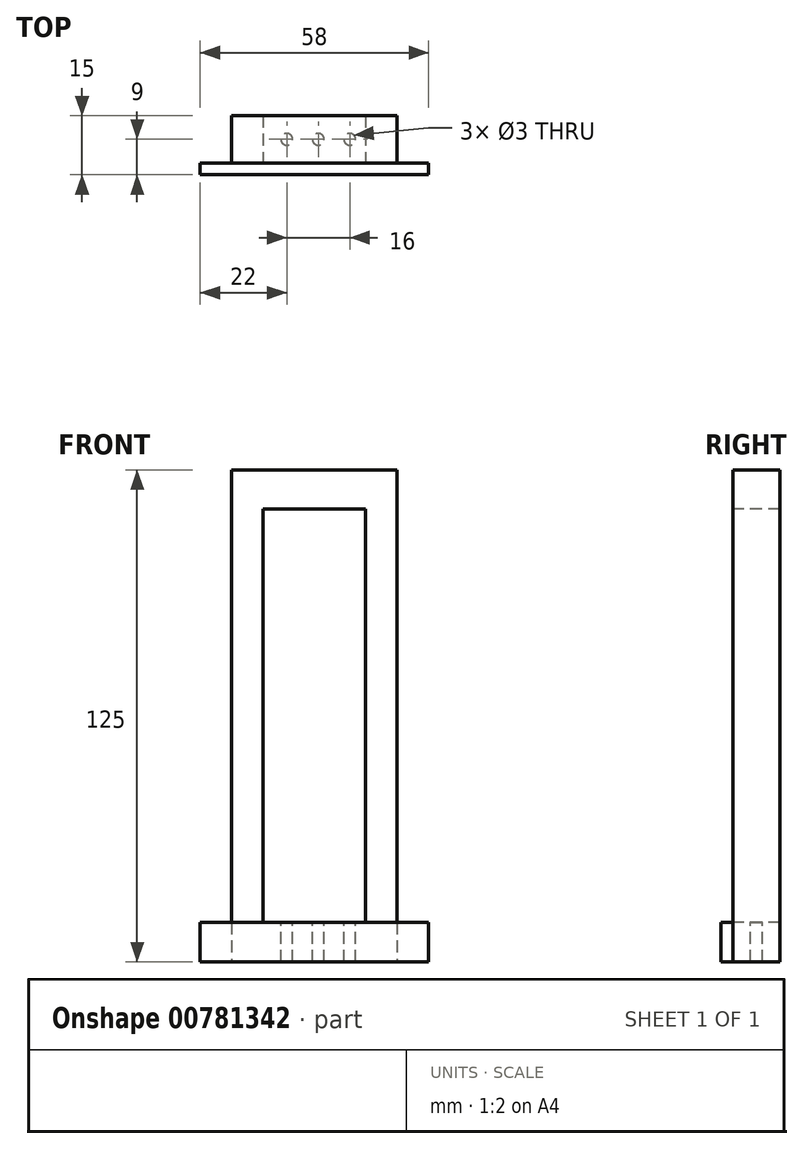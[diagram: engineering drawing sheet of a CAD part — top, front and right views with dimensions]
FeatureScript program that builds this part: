
annotation { "Feature Type Name" : "Feature", "Feature Type Description" : "" }
export const myFeature = defineFeature(function(context is Context, id is Id, definition is map)
    precondition{}
    {
        {
            var Q0;
            Q0=qCreatedBy(makeId("Top.planeOp"),FACE);
            var sketch = newSketch(context, id + "F0", { "sketchPlane" : qUnion([Q0])});
            skLineSegment(sketch, "E0.bottom", {"start": v(21, 6) * mm, "end": v(-21, 6) * mm});
            skLineSegment(sketch, "E0.top", {"start": v(21, -6) * mm, "end": v(-21, -6) * mm});
            skLineSegment(sketch, "E0.left", {"start": v(21, 6) * mm, "end": v(21, -6) * mm});
            skLineSegment(sketch, "E0.right", {"start": v(-21, 6) * mm, "end": v(-21, -6) * mm});
            skPoint(sketch, "E0.middle", {"position": v(0, 0) * mm});
            skSolve(sketch);
        }
        {
            var Q0;
            Q0 = qSketchRegion(id + "F0", true);
            extrude(context, id + "F1", {"entities" : qUnion([Q0]), "depth" : 10 * mm, "offsetDistance" : 25 * mm});
        }
        {
            var Q0;
            Q0=makeQuery(id+"F1.opExtrude","CAP_FACE",FACE,{"disambiguationData":[OSD([sQuery(id+"F0.wireOp",EDGE,"E0.bottom"),sQuery(id+"F0.wireOp",EDGE,"E0.top"),sQuery(id+"F0.wireOp",EDGE,"E0.left"),sQuery(id+"F0.wireOp",EDGE,"E0.right")])],"isStart":false});
            var sketch = newSketch(context, id + "F2", { "sketchPlane" : qUnion([Q0])});
            skLineSegment(sketch, "E1.bottom", {"start": v(-21, 6) * mm, "end": v(-13, 6) * mm});
            skLineSegment(sketch, "E1.top", {"start": v(-21, -6) * mm, "end": v(-13, -6) * mm});
            skLineSegment(sketch, "E1.left", {"start": v(-21, 6) * mm, "end": v(-21, -6) * mm});
            skLineSegment(sketch, "E1.right", {"start": v(-13, 6) * mm, "end": v(-13, -6) * mm});
            skLineSegment(sketch, "E2.bottom", {"start": v(21, 6) * mm, "end": v(13, 6) * mm});
            skLineSegment(sketch, "E2.top", {"start": v(21, -6) * mm, "end": v(13, -6) * mm});
            skLineSegment(sketch, "E2.left", {"start": v(21, 6) * mm, "end": v(21, -6) * mm});
            skLineSegment(sketch, "E2.right", {"start": v(13, 6) * mm, "end": v(13, -6) * mm});
            skSolve(sketch);
        }
        {
            var Q0;
            Q0 = qSketchRegion(id + "F2", true);
            extrude(context, id + "F3", {"entities" : qUnion([Q0]), "operationType" : NewBodyOperationType.ADD, "depth" : 105 * mm, "offsetDistance" : 25 * mm});
        }
        {
            var Q0;
            Q0=makeQuery(id+"F3.opExtrude","CAP_FACE",FACE,{"disambiguationData":[OSD([sQuery(id+"F2.wireOp",EDGE,"E1.bottom"),sQuery(id+"F2.wireOp",EDGE,"E1.top"),sQuery(id+"F2.wireOp",EDGE,"E1.left"),sQuery(id+"F2.wireOp",EDGE,"E1.right")])],"isStart":false});
            var sketch = newSketch(context, id + "F4", { "sketchPlane" : qUnion([Q0])});
            skLineSegment(sketch, "E3.bottom", {"start": v(-21, 6) * mm, "end": v(21, 6) * mm});
            skLineSegment(sketch, "E3.top", {"start": v(-21, -6) * mm, "end": v(21, -6) * mm});
            skLineSegment(sketch, "E3.left", {"start": v(-21, 6) * mm, "end": v(-21, -6) * mm});
            skLineSegment(sketch, "E3.right", {"start": v(21, 6) * mm, "end": v(21, -6) * mm});
            skSolve(sketch);
        }
        {
            var Q0;
            Q0 = qSketchRegion(id + "F4", true);
            extrude(context, id + "F5", {"entities" : qUnion([Q0]), "operationType" : NewBodyOperationType.ADD, "depth" : 10 * mm, "offsetDistance" : 25 * mm});
        }
        {
            var Q0;
            Q0=makeQuery(id+"F5.boolean.opBoolean","MERGE",FACE,{"derivedFrom":[makeQuery(id+"F3.boolean.opBoolean","MERGE",FACE,{"derivedFrom":[makeQuery(id+"F1.opExtrude","SWEPT_FACE",FACE,{"disambiguationData":[OSD([sQuery(id+"F0.wireOp",EDGE,"E0.top")])]}),makeQuery(id+"F3.opExtrude","SWEPT_FACE",FACE,{"disambiguationData":[OSD([sQuery(id+"F2.wireOp",EDGE,"E1.top")])]}),makeQuery(id+"F3.opExtrude","SWEPT_FACE",FACE,{"disambiguationData":[OSD([sQuery(id+"F2.wireOp",EDGE,"E2.top")])]})]}),makeQuery(id+"F5.opExtrude","SWEPT_FACE",FACE,{"disambiguationData":[OSD([sQuery(id+"F4.wireOp",EDGE,"E3.top")])]})]});
            var sketch = newSketch(context, id + "F6", { "sketchPlane" : qUnion([Q0])});
            skLineSegment(sketch, "E4.bottom", {"start": v(-29, 0) * mm, "end": v(29, 0) * mm});
            skLineSegment(sketch, "E4.top", {"start": v(-29, 10) * mm, "end": v(29, 10) * mm});
            skLineSegment(sketch, "E4.left", {"start": v(-29, 0) * mm, "end": v(-29, 10) * mm});
            skLineSegment(sketch, "E4.right", {"start": v(29, 0) * mm, "end": v(29, 10) * mm});
            skPoint(sketch, "E4.middle", {"position": v(0, 5) * mm});
            skSolve(sketch);
        }
        {
            var Q0;
            Q0 = qSketchRegion(id + "F6", true);
            extrude(context, id + "F7", {"entities" : qUnion([Q0]), "operationType" : NewBodyOperationType.ADD, "depth" : 3 * mm, "offsetDistance" : 25 * mm});
        }
        {
            var Q0;
            {var subQ0=sQuery(id+"F6.wireOp",EDGE,"E4.top");Q0=makeQuery(id+"FTLL2BZCXgbG7Gb_1.1.F7.boolean.opBoolean","MERGE",FACE,{"derivedFrom":[makeQuery(id+"F7.boolean.opBoolean","MERGE",FACE,{"derivedFrom":[makeQuery(id+"F1.opExtrude","CAP_FACE",FACE,{"disambiguationData":[OSD([sQuery(id+"F0.wireOp",EDGE,"E0.bottom"),sQuery(id+"F0.wireOp",EDGE,"E0.top"),sQuery(id+"F0.wireOp",EDGE,"E0.left"),sQuery(id+"F0.wireOp",EDGE,"E0.right")])],"isStart":false}),makeQuery(id+"F7.opExtrude","SWEPT_FACE",FACE,{"disambiguationData":[OSD([subQ0])]})]}),makeQuery(id+"FTLL2BZCXgbG7Gb_1.1.F7.opExtrude","SWEPT_FACE",FACE,{"disambiguationData":[OSD([subQ0])]})]});}
            var sketch = newSketch(context, id + "F8", { "sketchPlane" : qUnion([Q0])});
            skLineSegment(sketch, "E5", {"start": v(13, 0) * mm, "end": v(-13, 0) * mm, "construction": true});
            skCircle(sketch, "E6", {"center": v(-7, 0) * mm, "radius": 1.5 * mm});
            skCircle(sketch, "E7.1.0.0", {"center": v(1, 0) * mm, "radius": 1.5 * mm});
            skCircle(sketch, "E7.2.0.0", {"center": v(9, 0) * mm, "radius": 1.5 * mm});
            skLineSegment(sketch, "E7.direction1", {"start": v(-7, 0) * mm, "end": v(1, 0) * mm, "construction": true});
            skSolve(sketch);
        }
        {
            var Q0;
            Q0=makeQuery(id+"F8.imprint","IMPRINT",FACE,{"disambiguationData":[TD([[makeQuery(id+"F8.imprint","IMPRINT",EDGE,{"derivedFrom":sQuery(id+"F8.wireOp",EDGE,"E6")}),1.0]])]});
            var Q1;
            Q1=makeQuery(id+"F8.imprint","IMPRINT",FACE,{"disambiguationData":[TD([[makeQuery(id+"F8.imprint","IMPRINT",EDGE,{"derivedFrom":sQuery(id+"F8.wireOp",EDGE,"E7.1.0.0")}),1.0]])]});
            var Q2;
            Q2=makeQuery(id+"F8.imprint","IMPRINT",FACE,{"disambiguationData":[TD([[makeQuery(id+"F8.imprint","IMPRINT",EDGE,{"derivedFrom":sQuery(id+"F8.wireOp",EDGE,"E7.2.0.0")}),1.0]])]});
            extrude(context, id + "F9", {"entities" : qUnion([Q0, Q1, Q2]), "operationType" : NewBodyOperationType.REMOVE, "oppositeDirection" : true, "depth" : 10 * mm, "offsetDistance" : 25 * mm});
        }
    });
